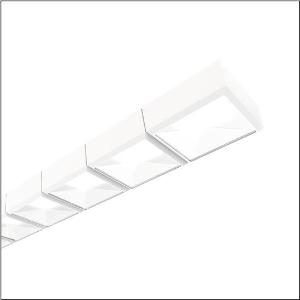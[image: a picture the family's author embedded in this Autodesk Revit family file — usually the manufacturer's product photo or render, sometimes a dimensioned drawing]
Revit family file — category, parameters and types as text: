
# Revit family: scriptus_11_5mz223d04wa
name_source: partatom
category: Lighting Fixtures
units: mm (PartAtom-declared; Revit-internal decimal feet)

## family parameters
Cut with Voids When Loaded = No
Host = Face
Light Source = No
Part Type = Normal
Room Calculation Point = No
Round Connector Dimension = Use Diameter
Shared = No

## types (1)
- --- (1 x LED 4000K / CRI = 80 (unbekannt), 7230 lm, 4000K)
    Apparent Load = 51 VA
    CIE Flux Codes = 82 95 99 100 100
    Color Rendering = 80
    Color Temperature = 4000K
    Default Elevation = 1800 mm
    Description = Scriptus 11, office luminaire, primary optical cover: lenses, CAT 2 (L<= 3000cd/m²), light emission: direct distribution, primary light characteristic: symmetric, installation type: surface-mounted, LED, rated luminous flux: 7.230lm, luminous efficacy: 143lm/W, light colour: 840, colour temperature: 4000K, control gear: DALI, with terminal, 5-pole, mains connection: 230V, AC, 50Hz, rated input power: 51W, housing, luminaire housing, of aluminium, traffic white (RAL 9016), length: 2.426mm, width: 114mm, height: 57mm, protection rating (complete): IP20, insulation class (complete): insulation class I (protective earthing), certification: CE, ENEC, VDE, protection symbol: F, permissible operating ambient temperature: 0..+35°C, standard: EN 50419, packaging unit: 1 piece
    Height = 57 mm
    Lamp = 1 x LED 4000K / CRI >= 80 (unbekannt)
    Lamp Light Flux = 7230 lm
    Lamp count = 1
    Length = 2426 mm
    Luminous efficacy = 143 lm/W
    Manufacturer = Siteco
    ModVariant = No
    Model = 5MZ223D04WA
    Mounting Place = Ceiling
    Mounting Type = Surface mounted
    Number of Poles = 1
    OnlyDefault = Yes
    Power Factor = 1
    Product Name = Scriptus 11
    Product group = office luminaire | ceiling mounted
    ProductGroupID = 301
    Protection Class = Protection class I
    Protection Degree = IP 20
    RLX_Detail_Level = 1
    RLX_Emergency_Light_Flux = 0 lm
    RLX_Emergency_Type = 0
    RLX_Emergency_Type_DB = No
    RlxData = <blob elided: 31341 chars, md5=5cf25a0e>
    Socket = socket
    Standby Power = 0 W
    System Light Flux = 7230 lm
    System Power = 51 W
    Type Comments = factory setting: luminous flux: 100 % | dim-lin: 254 | 525 mA
    Type Image = l_1004833.jpg
    URL = http://relux.com
    VarID = @adj_197887
    Voltage = 0 V
    Weight = 0.00 kg
    Width = 114 mm

## geometry (parser evidence)
native form markers: Blend x4, Sweep x11
no freeform markers — native parametric forms only
